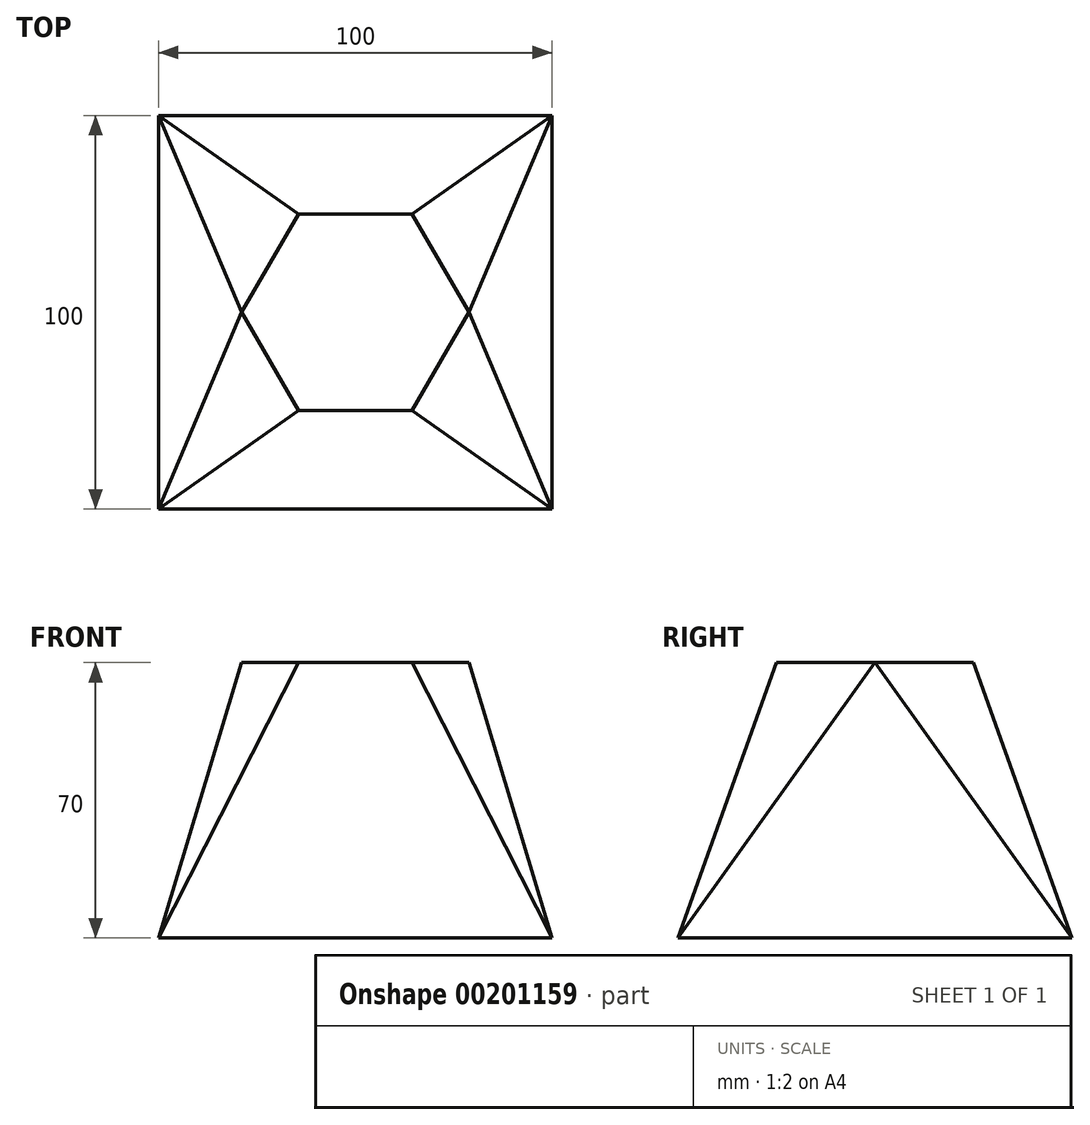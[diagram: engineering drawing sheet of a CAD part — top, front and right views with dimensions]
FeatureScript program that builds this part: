
annotation { "Feature Type Name" : "Feature", "Feature Type Description" : "" }
export const myFeature = defineFeature(function(context is Context, id is Id, definition is map)
    precondition{}
    {
        {
            var Q0;
            Q0=qCreatedBy(makeId("Top.planeOp"),FACE);
            var sketch = newSketch(context, id + "F0", { "sketchPlane" : qUnion([Q0])});
            skLineSegment(sketch, "E0.bottom", {"start": v(-50, 50) * mm, "end": v(50, 50) * mm});
            skLineSegment(sketch, "E0.top", {"start": v(-50, -50) * mm, "end": v(50, -50) * mm});
            skLineSegment(sketch, "E0.left", {"start": v(-50, 50) * mm, "end": v(-50, -50) * mm});
            skLineSegment(sketch, "E0.right", {"start": v(50, 50) * mm, "end": v(50, -50) * mm});
            skPoint(sketch, "E0.middle", {"position": v(0, 0) * mm});
            skSolve(sketch);
        }
        {
            var Q0;
            Q0=qCreatedBy(makeId("Top.planeOp"),FACE);
            cPlane(context, id + "F1", {"entities" : qUnion([Q0]), "cplaneType" : CPlaneType.OFFSET, "offset" : 70 * mm, "width" : 150 * mm, "height" : 150 * mm});
        }
        {
            var Q0;
            Q0=qCreatedBy(id+"F1.planeOp",FACE);
            var sketch = newSketch(context, id + "F2", { "sketchPlane" : qUnion([Q0])});
            skCircle(sketch, "E1.cCircle", {"center": v(0, 0) * mm, "radius": 25 * mm, "construction": true});
            skLineSegment(sketch, "E1.0", {"start": v(-14.43, 25) * mm, "end": v(14.43, 25) * mm});
            skLineSegment(sketch, "E1.1", {"start": v(14.43, 25) * mm, "end": v(28.87, 0) * mm});
            skLineSegment(sketch, "E1.2", {"start": v(28.87, 0) * mm, "end": v(14.43, -25) * mm});
            skLineSegment(sketch, "E1.3", {"start": v(14.43, -25) * mm, "end": v(-14.43, -25) * mm});
            skLineSegment(sketch, "E1.4", {"start": v(-14.43, -25) * mm, "end": v(-28.87, 0) * mm});
            skLineSegment(sketch, "E1.5", {"start": v(-28.87, 0) * mm, "end": v(-14.43, 25) * mm});
            skPoint(sketch, "E1.0.midPoint", {"position": v(0, 25) * mm});
            skLineSegment(sketch, "E2", {"start": v(-14.43, 25) * mm, "end": v(-14.43, -25) * mm});
            skLineSegment(sketch, "E3", {"start": v(14.43, 25) * mm, "end": v(14.43, -25) * mm});
            skSolve(sketch);
        }
        {
            var Q0;
            Q0=qCreatedBy(id+"F1.planeOp",FACE);
            var sketch = newSketch(context, id + "F3", { "sketchPlane" : qUnion([Q0])});
            skLineSegment(sketch, "E4.bottom", {"start": v(-14.43, 25) * mm, "end": v(14.43, 25) * mm});
            skLineSegment(sketch, "E4.top", {"start": v(-14.43, -25) * mm, "end": v(14.43, -25) * mm});
            skLineSegment(sketch, "E4.left", {"start": v(-14.43, 25) * mm, "end": v(-14.43, -25) * mm});
            skLineSegment(sketch, "E4.right", {"start": v(14.43, 25) * mm, "end": v(14.43, -25) * mm});
            skPoint(sketch, "E4.middle", {"position": v(0, 0) * mm});
            skSolve(sketch);
        }
        {
            var Q0;
            Q0=makeQuery(id+"F3.imprint","IMPRINT",FACE,{"disambiguationData":[TD([[makeQuery(id+"F3.imprint","IMPRINT",EDGE,{"derivedFrom":sQuery(id+"F3.wireOp",EDGE,"E4.bottom")}),-1.0]])]});
            var Q1;
            Q1=makeQuery(id+"F0.imprint","IMPRINT",FACE,{"disambiguationData":[TD([[makeQuery(id+"F0.imprint","IMPRINT",EDGE,{"derivedFrom":sQuery(id+"F0.wireOp",EDGE,"E0.bottom")}),-1.0]])]});
            loft(context, id + "F4", {"sheetProfilesArray" : [{ "sheetProfileEntities" : qUnion([Q0]) }, { "sheetProfileEntities" : qUnion([Q1]) }]});
        }
        {
            var Q1;
            Q1=makeQuery(id+"F2.imprint","IMPRINT",FACE,{"disambiguationData":[TD([[makeQuery(id+"F2.imprint","IMPRINT",EDGE,{"derivedFrom":sQuery(id+"F2.wireOp",EDGE,"E1.4")}),-1.0]])]});
            var Q2;
            Q2=makeQuery(id+"F4.opLoft","MID_CAP_VERTEX",VERTEX,{"disambiguationData":[OSD([sQuery(id+"F0.wireOp",EDGE,"E0.bottom"),sQuery(id+"F0.wireOp",EDGE,"E0.left")])],"capPos":1.0});
            loft(context, id + "F5", {"operationType" : NewBodyOperationType.ADD, "sheetProfilesArray" : [{ "sheetProfileEntities" : qUnion([Q1]) }, { "sheetProfileEntities" : qUnion([Q2]) }]});
        }
        {
            var Q1;
            Q1=makeQuery(id+"F4.opLoft","MID_CAP_VERTEX",VERTEX,{"disambiguationData":[OSD([sQuery(id+"F0.wireOp",EDGE,"E0.top"),sQuery(id+"F0.wireOp",EDGE,"E0.left")])],"capPos":1.0});
            var Q2;
            Q2=makeQuery(id+"F2.imprint","IMPRINT",FACE,{"disambiguationData":[TD([[makeQuery(id+"F2.imprint","IMPRINT",EDGE,{"derivedFrom":sQuery(id+"F2.wireOp",EDGE,"E1.4")}),-1.0]])]});
            loft(context, id + "F6", {"operationType" : NewBodyOperationType.ADD, "sheetProfilesArray" : [{ "sheetProfileEntities" : qUnion([Q1]) }, { "sheetProfileEntities" : qUnion([Q2]) }]});
        }
        {
            var Q1;
            Q1=makeQuery(id+"F6.opLoft","SWEPT_FACE",FACE,{"disambiguationData":[OSD([sQuery(id+"F2.wireOp",EDGE,"E1.0"),sQuery(id+"F2.wireOp",EDGE,"E1.4"),sQuery(id+"F2.wireOp",EDGE,"E1.5"),sQuery(id+"F2.wireOp",EDGE,"E2")])]});
            var Q2;
            Q2=makeQuery(id+"F5.opLoft","SWEPT_FACE",FACE,{"disambiguationData":[OSD([sQuery(id+"F2.wireOp",EDGE,"E1.3"),sQuery(id+"F2.wireOp",EDGE,"E1.4"),sQuery(id+"F2.wireOp",EDGE,"E1.5"),sQuery(id+"F2.wireOp",EDGE,"E2")])]});
            var Q3;
            Q3=makeQuery(id+"F4.opLoft","MID_CAP_EDGE",EDGE,{"disambiguationData":[OSD([sQuery(id+"F0.wireOp",EDGE,"E0.bottom"),sQuery(id+"F0.wireOp",EDGE,"E0.top"),sQuery(id+"F0.wireOp",EDGE,"E0.left")])],"capPos":1.0});
            loft(context, id + "F7", {"operationType" : NewBodyOperationType.ADD, "addGuides" : true, "sheetProfilesArray" : [{ "sheetProfileEntities" : qUnion([Q1]) }, { "sheetProfileEntities" : qUnion([Q2]) }], "guidesArray" : [{ "guideEntities" : qUnion([Q3]), "guideDerivativeType" : LoftGuideDerivativeType.DEFAULT, "guideDerivativeMagnitude" : 1 }]});
        }
        {
            var Q1;
            Q1=makeQuery(id+"F2.imprint","IMPRINT",FACE,{"disambiguationData":[TD([[makeQuery(id+"F2.imprint","IMPRINT",EDGE,{"derivedFrom":sQuery(id+"F2.wireOp",EDGE,"E1.1")}),-1.0]])]});
            var Q2;
            Q2=makeQuery(id+"F4.opLoft","MID_CAP_VERTEX",VERTEX,{"disambiguationData":[OSD([sQuery(id+"F0.wireOp",EDGE,"E0.top"),sQuery(id+"F0.wireOp",EDGE,"E0.right")])],"capPos":1.0});
            loft(context, id + "F8", {"operationType" : NewBodyOperationType.ADD, "sheetProfilesArray" : [{ "sheetProfileEntities" : qUnion([Q1]) }, { "sheetProfileEntities" : qUnion([Q2]) }]});
        }
        {
            var Q1;
            Q1=makeQuery(id+"F2.imprint","IMPRINT",FACE,{"disambiguationData":[TD([[makeQuery(id+"F2.imprint","IMPRINT",EDGE,{"derivedFrom":sQuery(id+"F2.wireOp",EDGE,"E1.1")}),-1.0]])]});
            var Q2;
            Q2=makeQuery(id+"F4.opLoft","MID_CAP_VERTEX",VERTEX,{"disambiguationData":[OSD([sQuery(id+"F0.wireOp",EDGE,"E0.bottom"),sQuery(id+"F0.wireOp",EDGE,"E0.right")])],"capPos":1.0});
            loft(context, id + "F9", {"operationType" : NewBodyOperationType.ADD, "sheetProfilesArray" : [{ "sheetProfileEntities" : qUnion([Q1]) }, { "sheetProfileEntities" : qUnion([Q2]) }]});
        }
        {
            var Q1;
            Q1=makeQuery(id+"F9.opLoft","SWEPT_FACE",FACE,{"disambiguationData":[OSD([sQuery(id+"F2.wireOp",EDGE,"E1.1"),sQuery(id+"F2.wireOp",EDGE,"E1.2"),sQuery(id+"F2.wireOp",EDGE,"E1.3"),sQuery(id+"F2.wireOp",EDGE,"E3")])]});
            var Q2;
            Q2=makeQuery(id+"F8.opLoft","SWEPT_FACE",FACE,{"disambiguationData":[OSD([sQuery(id+"F2.wireOp",EDGE,"E1.0"),sQuery(id+"F2.wireOp",EDGE,"E1.1"),sQuery(id+"F2.wireOp",EDGE,"E1.2"),sQuery(id+"F2.wireOp",EDGE,"E3")])]});
            var Q3;
            Q3=makeQuery(id+"F4.opLoft","MID_CAP_EDGE",EDGE,{"disambiguationData":[OSD([sQuery(id+"F0.wireOp",EDGE,"E0.bottom"),sQuery(id+"F0.wireOp",EDGE,"E0.top"),sQuery(id+"F0.wireOp",EDGE,"E0.right")])],"capPos":1.0});
            loft(context, id + "F10", {"operationType" : NewBodyOperationType.ADD, "addGuides" : true, "sheetProfilesArray" : [{ "sheetProfileEntities" : qUnion([Q1]) }, { "sheetProfileEntities" : qUnion([Q2]) }], "guidesArray" : [{ "guideEntities" : qUnion([Q3]), "guideDerivativeType" : LoftGuideDerivativeType.DEFAULT, "guideDerivativeMagnitude" : 1 }]});
        }
    });
